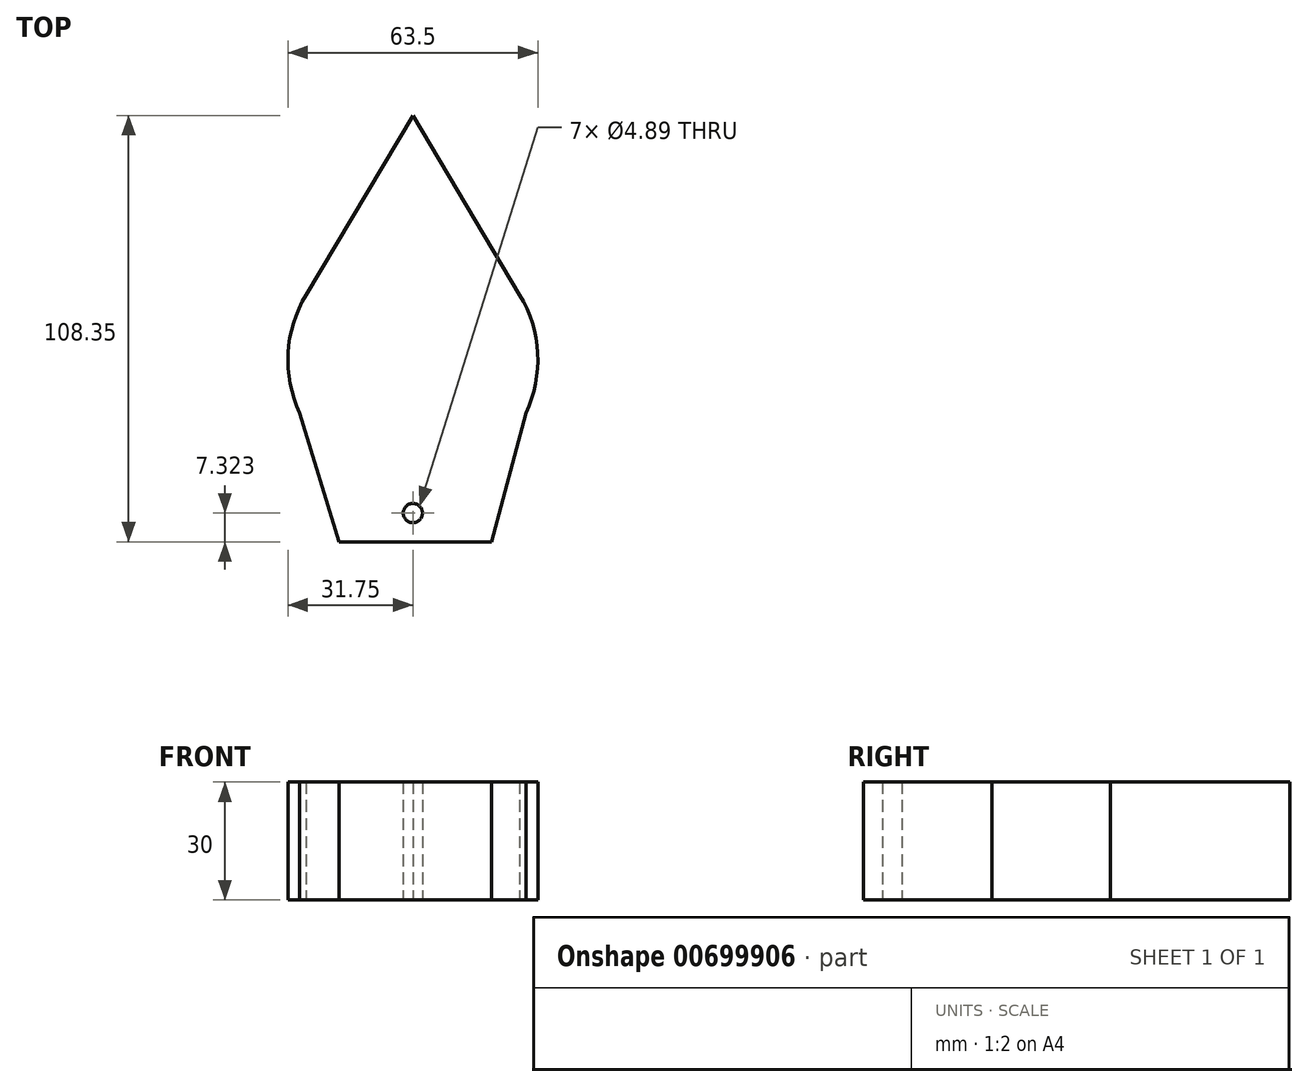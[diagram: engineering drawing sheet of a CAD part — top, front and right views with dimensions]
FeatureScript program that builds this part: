
annotation { "Feature Type Name" : "Feature", "Feature Type Description" : "" }
export const myFeature = defineFeature(function(context is Context, id is Id, definition is map)
    precondition{}
    {
        {
            var Q0;
            Q0=qCreatedBy(makeId("Top.planeOp"),FACE);
            var sketch = newSketch(context, id + "F0", { "sketchPlane" : qUnion([Q0])});
            skCircle(sketch, "E0", {"center": v(0, 0) * mm, "radius": 31.75 * mm});
            skLineSegment(sketch, "E1", {"start": v(-27.12, 16.5) * mm, "end": v(0, 62.11) * mm});
            skLineSegment(sketch, "E2", {"start": v(0, 62.11) * mm, "end": v(27.12, 16.5) * mm});
            skLineSegment(sketch, "E3", {"start": v(-28.72, -13.53) * mm, "end": v(-18.77, -46.24) * mm});
            skLineSegment(sketch, "E4", {"start": v(28.72, -13.53) * mm, "end": v(20, -46.24) * mm});
            skLineSegment(sketch, "E5", {"start": v(20, -46.24) * mm, "end": v(-18.77, -46.24) * mm});
            skPoint(sketch, "E6", {"position": v(0, -38.92) * mm});
            skCircle(sketch, "E7", {"center": v(0, -38.92) * mm, "radius": 2.44 * mm});
            skSolve(sketch);
        }
        {
            var Q0;
            {var subQ0=sQuery(id+"F0.wireOp",EDGE,"E0");var subQ1=makeQuery(id+"F0.imprint","INTERSECT",VERTEX,{"derivedFrom":[subQ0,sQuery(id+"F0.wireOp",EDGE,"E1")]});Q0=makeQuery(id+"F0.imprint","IMPRINT",FACE,{"disambiguationData":[TD([[makeQuery(id+"F0.imprint","IMPRINT",EDGE,{"disambiguationData":[TD([[subQ1,1.0]])],"derivedFrom":subQ0}),1.0]])]});}
            var Q1;
            {var subQ0=sQuery(id+"F0.wireOp",EDGE,"E1");Q1=makeQuery(id+"F0.imprint","IMPRINT",FACE,{"disambiguationData":[TD([[makeQuery(id+"F0.imprint","IMPRINT",EDGE,{"derivedFrom":subQ0}),-1.0]])]});}
            var Q2;
            {var subQ0=sQuery(id+"F0.wireOp",EDGE,"E3");Q2=makeQuery(id+"F0.imprint","IMPRINT",FACE,{"disambiguationData":[TD([[makeQuery(id+"F0.imprint","IMPRINT",EDGE,{"derivedFrom":subQ0}),1.0]])]});}
            extrude(context, id + "F1", {"entities" : qUnion([Q0, Q1, Q2]), "depth" : 30 * mm, "offsetDistance" : 25 * mm});
        }
    });
